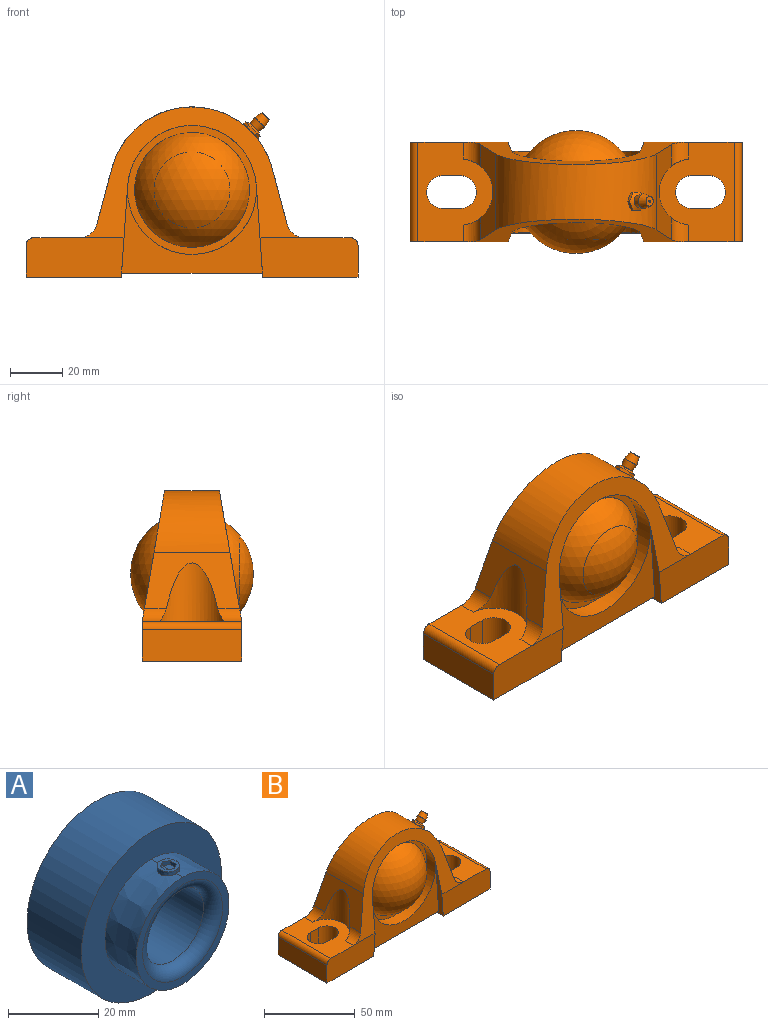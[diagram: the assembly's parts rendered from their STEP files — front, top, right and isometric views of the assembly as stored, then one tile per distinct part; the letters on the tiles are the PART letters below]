
ASSEMBLY  parts=2 mates=1
PART A: 23 faces, bbox 43.8x31x43.8 mm
  f0: extruded ~29.01x14.5mm, area 436.2mm2, adj f1,f2,f7,f18
  f1: extruded ~29.01x14.5mm, area 436.2mm2, adj f0,f2,f7,f17
  f2: plane 29.01x29.01mm, normal (0,-1,0), area 168mm2, adj f0,f1,f9
  f3: extruded ~29.01x14.5mm, area 191.5mm2, adj f4,f6,f8
  f4: extruded ~29.01x14.5mm, area 191.5mm2, adj f3,f6,f8
  f5: cylinder r=9.53mm len=24.99mm, axis (0,1,0), area 1495.5mm2, adj f9,f10
  f6: plane 29.01x29.01mm, normal (0,1,0), area 168mm2, adj f3,f4,f10
  f7: plane 43.82x43.82mm, normal (0,-1,0), area 847.3mm2, adj f0,f1,f11
  f8: plane 43.82x43.82mm, normal (0,1,0), area 847.3mm2, adj f3,f4,f11
  f9: torus R=12.53mm, axis (0,-1,0), area 314.3mm2, adj f2,f5
  f10: torus R=12.53mm, axis (0,1,0), area 314.3mm2, adj f5,f6
  f11: cylinder r=21.91mm len=43.82mm, axis (0,1,0), area 2339.3mm2, adj f7,f8
  f12: plane 1.83x1.08mm, normal (1,0,0), area 2mm2, adj f13,f19,f20,f22
  f13: plane 1.59x1.08mm, normal (0.5,-0.87,0), area 1.9mm2, adj f12,f14,f20,f22
  f14: plane 1.59x1.08mm, normal (-0.5,-0.87,0), area 1.9mm2, adj f13,f15,f20,f21
  f15: plane 1.83x1.08mm, normal (-1,0,0), area 2mm2, adj f14,f16,f20,f21
  f16: plane 1.59x1.08mm, normal (-0.5,0.87,0), area 1.9mm2, adj f15,f19,f20,f21
  f17: extruded ~4.98x2.49mm, area 7.7mm2, adj f1,f18,f20
  f18: extruded ~4.98x2.49mm, area 7.7mm2, adj f0,f17,f20
  f19: plane 1.59x1.08mm, normal (0.5,0.87,0), area 1.9mm2, adj f12,f16,f20,f22
  f20: plane 4.98x4.98mm, normal (0,0,1), area 10.7mm2, adj f12,f13,f14,f15,f16,f17,f18,f19
  f21: extruded ~3.67x1.59mm, area 4.4mm2, adj f14,f15,f16,f22
  f22: extruded ~3.67x1.59mm, area 4.4mm2, adj f12,f13,f19,f21
PART B: 65 faces, bbox 137.5x57.6x75.6 mm
  f0: sphere r=23.53mm, area 2225.6mm2, adj f1
  f1: plane 59.86x59.86mm, normal (0,-1,0), area 400.9mm2, adj f0,f2
  f2: cylinder r=24.68mm len=49.35mm, axis (0,1,0), area 921mm2, adj f1,f3,f4
  f3: plane 53.92x33.55mm, normal (0,-1,0), area 689.1mm2, adj f2,f5,f6,f7
  f4: plane 86.32x50.39mm, normal (0,-0.99,0.17), area 1021.2mm2, adj f2,f5,f6,f8,f9,f10,f11,f12
  f5: plane 38.1x35.06mm, normal (1,0,-0.07), area 218.9mm2, adj f3,f4,f7,f14,f15,f16,f17,f18
  f6: plane 38.1x35.06mm, normal (-1,0,-0.07), area 218.9mm2, adj f3,f4,f7,f8,f17,f18,f19,f20
  f7: plane 53.92x31.27mm, normal (0,0,-1), area 1686.2mm2, adj f3,f5,f6,f18
  f8: plane 37.49x15.08mm, normal (0,-1,0), area 555.5mm2, adj f4,f6,f20,f21,f22,f23
  f9: cylinder r=6.79mm len=9.22mm, axis (0,-1,0), area 65.7mm2, adj f4,f10,f23,f24
  f10: plane 36.38x21.44mm, normal (0.97,0,0.26), area 479.7mm2, adj f4,f9,f11,f17,f24,f25
  f11: cylinder r=31.75mm len=61.34mm, axis (0,1,0), area 1962.3mm2, adj f4,f10,f12,f17,f26
  f12: plane 36.38x21.44mm, normal (-0.97,0,0.26), area 479.7mm2, adj f4,f11,f13,f17,f27,f28
  f13: cylinder r=6.79mm len=9.22mm, axis (0,1,0), area 65.7mm2, adj f4,f12,f27,f29
  f14: plane 37.49x15.08mm, normal (0,-1,0), area 555.5mm2, adj f4,f5,f15,f29,f30,f31
  f15: plane 38.1x36.43mm, normal (0,0,-1), area 1180.8mm2, adj f5,f14,f16,f31,f32,f33,f34,f35
  f16: plane 37.49x15.08mm, normal (0,1,0), area 555.5mm2, adj f5,f15,f17,f29,f30,f31
  f17: plane 86.32x50.39mm, normal (0,0.99,0.17), area 1021.2mm2, adj f5,f6,f10,f11,f12,f16,f19,f25
  f18: plane 53.92x33.55mm, normal (0,1,0), area 689.1mm2, adj f5,f6,f7,f36
  f19: plane 37.49x15.08mm, normal (0,1,0), area 555.5mm2, adj f6,f17,f20,f21,f22,f23
  f20: plane 38.1x36.43mm, normal (0,0,-1), area 1180.8mm2, adj f6,f8,f19,f21,f37,f38,f39,f40
  f21: plane 38.1x12.07mm, normal (1,0,0), area 459.7mm2, adj f8,f19,f20,f22
  f22: cylinder r=3.02mm len=38.1mm, axis (0,1,0), area 180.5mm2, adj f8,f19,f21,f23
  f23: plane 38.1x28.73mm, normal (0,0,1), area 675.8mm2, adj f8,f9,f19,f22,f24,f25,f37,f38
  f24: cylinder r=12.7mm len=25.23mm, axis (0,0,-1), area 407mm2, adj f9,f10,f23,f25
  f25: cylinder r=6.79mm len=9.22mm, axis (0,-1,0), area 65.7mm2, adj f10,f17,f23,f24
  f26: cylinder r=3.17mm len=6.35mm, axis (0.71,0,0.71), area 2.1mm2, adj f11,f41
  f27: cylinder r=12.7mm len=25.23mm, axis (0,0,-1), area 407mm2, adj f12,f13,f28,f29
  f28: cylinder r=6.79mm len=9.22mm, axis (0,1,0), area 65.7mm2, adj f12,f17,f27,f29
  f29: plane 38.1x28.73mm, normal (0,0,1), area 675.8mm2, adj f13,f14,f16,f27,f28,f30,f32,f33
  f30: cylinder r=3.02mm len=38.1mm, axis (0,1,0), area 180.5mm2, adj f14,f16,f29,f31
  f31: plane 38.1x12.07mm, normal (-1,0,0), area 459.7mm2, adj f14,f15,f16,f30
  f32: plane 15.08x6.35mm, normal (0,-1,0), area 95.8mm2, adj f15,f29,f33,f35
  f33: cylinder r=6.35mm len=15.08mm, axis (0,0,1), area 300.9mm2, adj f15,f29,f32,f34
  f34: plane 15.08x6.35mm, normal (0,1,0), area 95.8mm2, adj f15,f29,f33,f35
  f35: cylinder r=6.35mm len=15.08mm, axis (0,0,1), area 300.9mm2, adj f15,f29,f32,f34
  f36: cylinder r=24.68mm len=49.35mm, axis (0,-1,0), area 921mm2, adj f17,f18,f42
  f37: plane 15.08x6.35mm, normal (0,-1,0), area 95.8mm2, adj f20,f23,f38,f40
  f38: cylinder r=6.35mm len=15.08mm, axis (0,0,1), area 300.9mm2, adj f20,f23,f37,f39
  f39: plane 15.08x6.35mm, normal (0,1,0), area 95.8mm2, adj f20,f23,f38,f40
  f40: cylinder r=6.35mm len=15.08mm, axis (0,0,1), area 300.9mm2, adj f20,f23,f37,f39
  f41: plane 6.99x4.94mm, normal (-0.71,0,-0.71), area 6.7mm2, adj f26,f43,f44,f45,f46,f47,f48
  f42: plane 59.86x59.86mm, normal (0,1,0), area 400.9mm2, adj f36,f49
  f43: cone r=3.76mm half-angle=60deg, axis (0.71,0,0.71), area 1.2mm2, adj f41,f50,f51
  f44: cone r=3.76mm half-angle=60deg, axis (0.71,0,0.71), area 1.2mm2, adj f41,f51,f52
  f45: cone r=3.76mm half-angle=60deg, axis (0.71,0,0.71), area 1.2mm2, adj f41,f52,f53
  f46: cone r=3.76mm half-angle=60deg, axis (0.71,0,0.71), area 1.2mm2, adj f41,f53,f54
  f47: cone r=3.76mm half-angle=60deg, axis (0.71,0,0.71), area 1.2mm2, adj f41,f54,f55
  f48: cone r=3.76mm half-angle=60deg, axis (0.71,0,0.71), area 1.2mm2, adj f41,f50,f55
  f49: sphere r=23.53mm, area 2225.6mm2, adj f42
  f50: plane 4.74x3.17mm, normal (0.61,-0.5,-0.61), area 4.5mm2, adj f43,f48,f51,f55,f56
  f51: plane 4.59x4.59mm, normal (0,-1,0), area 4.5mm2, adj f43,f44,f50,f52,f56
  f52: plane 4.74x3.17mm, normal (-0.61,-0.5,0.61), area 4.5mm2, adj f44,f45,f51,f53,f56
  f53: plane 4.74x3.17mm, normal (-0.61,0.5,0.61), area 4.5mm2, adj f45,f46,f52,f54,f56
  f54: plane 4.59x4.59mm, normal (0,1,0), area 4.5mm2, adj f46,f47,f53,f55,f56
  f55: plane 4.74x3.17mm, normal (0.61,0.5,-0.61), area 4.5mm2, adj f47,f48,f50,f54,f56
  f56: cone r=3.17mm half-angle=60deg, axis (-0.71,0,-0.71), area 39.8mm2, adj f50,f51,f52,f53,f54,f55,f57
  f57: cone r=2.55mm half-angle=10deg, axis (0.71,0,0.71), area 45.7mm2, adj f56,f58
  f58: cone r=2.36mm half-angle=15deg, axis (-0.71,0,-0.71), area 49.4mm2, adj f57,f59
  f59: plane 3.86x2.73mm, normal (0.71,0,0.71), area 11.2mm2, adj f58,f60
  f60: sphere r=0.56mm, area 0.6mm2, adj f59
  f61: plane 4.83x3.41mm, normal (-0.71,0,-0.71), area 18.3mm2, adj f62
  f62: cone r=2.79mm half-angle=45deg, axis (0.71,0,0.71), area 18.9mm2, adj f61,f63
  f63: cylinder r=3.17mm len=7.71mm, axis (0.71,0,0.71), area 80.8mm2, adj f62,f64
  f64: sphere r=23.53mm, area 17mm2, adj f63
PLACE A at identity
PLACE B at identity fixed
MATE revolute A.f9 <-> B.f11  axis (0,-1,0) through (47.63,-8.5,33.34)mm
